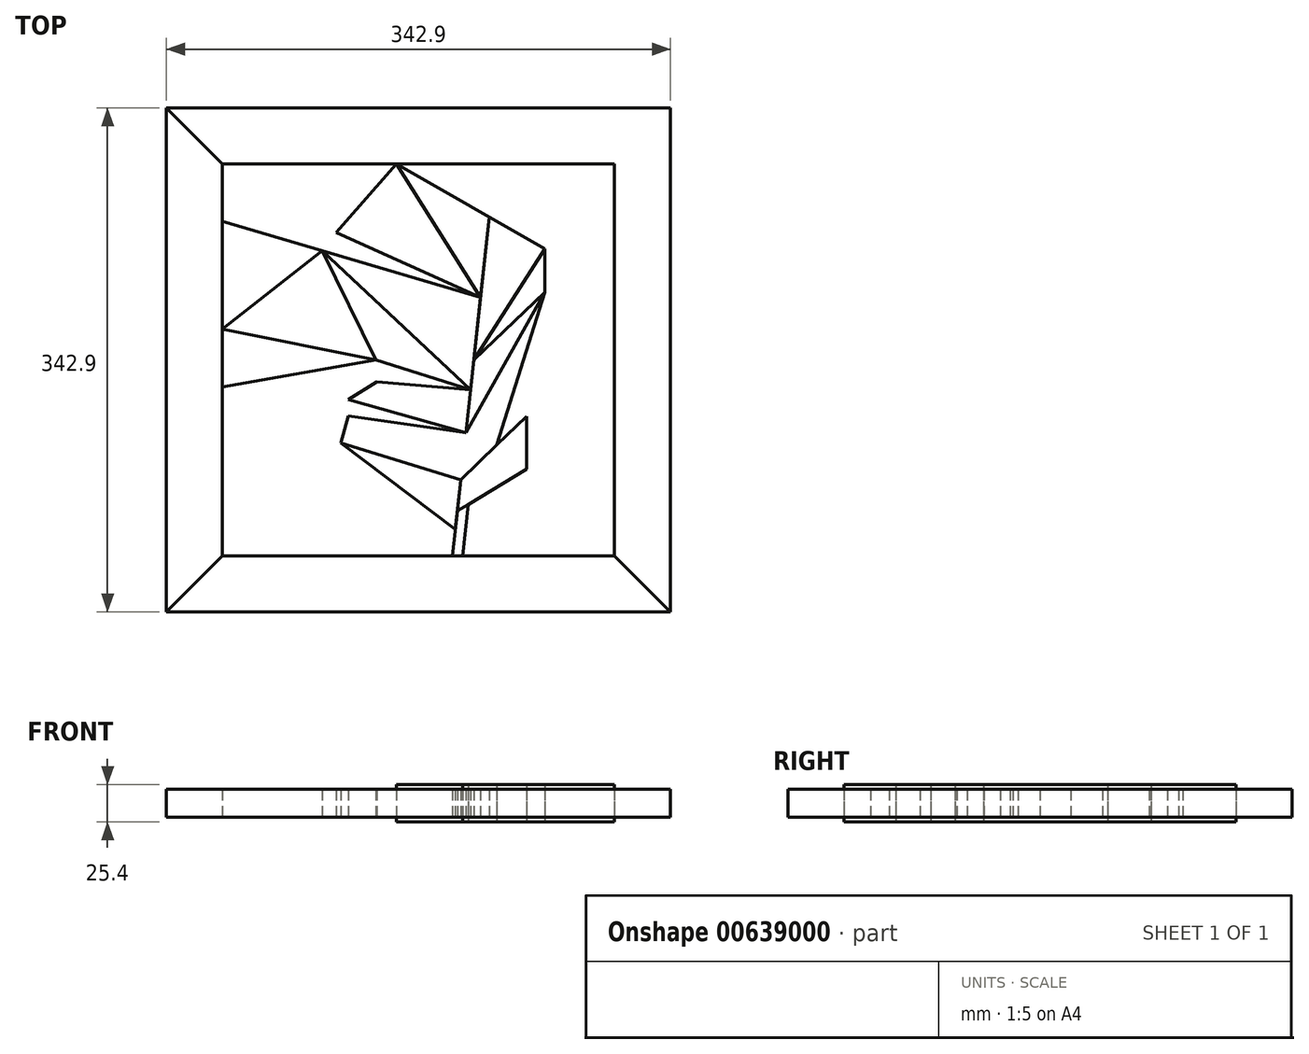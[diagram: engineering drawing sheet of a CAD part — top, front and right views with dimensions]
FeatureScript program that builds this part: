
annotation { "Feature Type Name" : "Feature", "Feature Type Description" : "" }
export const myFeature = defineFeature(function(context is Context, id is Id, definition is map)
    precondition{}
    {
        {
            var Q0;
            Q0=qCreatedBy(makeId("Top.planeOp"),FACE);
            var sketch = newSketch(context, id + "F0", { "sketchPlane" : qUnion([Q0])});
            skLineSegment(sketch, "E0.bottom", {"start": v(-171.45, -171.45) * mm, "end": v(171.45, -171.45) * mm});
            skLineSegment(sketch, "E0.top", {"start": v(-171.45, 171.45) * mm, "end": v(171.45, 171.45) * mm});
            skLineSegment(sketch, "E0.left", {"start": v(-171.45, -171.45) * mm, "end": v(-171.45, 171.45) * mm});
            skLineSegment(sketch, "E0.right", {"start": v(171.45, -171.45) * mm, "end": v(171.45, 171.45) * mm});
            skPoint(sketch, "E0.middle", {"position": v(0, 0) * mm});
            skLineSegment(sketch, "E1", {"start": v(-171.45, 171.45) * mm, "end": v(-133.35, 133.35) * mm});
            skLineSegment(sketch, "E2", {"start": v(-133.35, 133.35) * mm, "end": v(-133.35, -133.35) * mm});
            skLineSegment(sketch, "E3", {"start": v(-133.35, -133.35) * mm, "end": v(-171.45, -171.45) * mm});
            skLineSegment(sketch, "E4", {"start": v(-133.35, 133.35) * mm, "end": v(133.35, 133.35) * mm});
            skLineSegment(sketch, "E5", {"start": v(133.35, 133.35) * mm, "end": v(171.45, 171.45) * mm});
            skLineSegment(sketch, "E6", {"start": v(133.35, 133.35) * mm, "end": v(133.35, -133.35) * mm});
            skLineSegment(sketch, "E7", {"start": v(133.35, -133.35) * mm, "end": v(171.45, -171.45) * mm});
            skLineSegment(sketch, "E8", {"start": v(133.35, -133.35) * mm, "end": v(-133.35, -133.35) * mm});
            skLineSegment(sketch, "E9", {"start": v(-15.08, 133.35) * mm, "end": v(86.05, 75.46) * mm});
            skLineSegment(sketch, "E10", {"start": v(86.05, 75.46) * mm, "end": v(86.05, 45.93) * mm});
            skLineSegment(sketch, "E11", {"start": v(86.05, 45.93) * mm, "end": v(53.37, -57.95) * mm});
            skLineSegment(sketch, "E12", {"start": v(73.71, -38.4) * mm, "end": v(73.71, -74.27) * mm});
            skLineSegment(sketch, "E13", {"start": v(-15.08, 133.35) * mm, "end": v(-56.02, 86.54) * mm});
            skLineSegment(sketch, "E14", {"start": v(48.18, 97.13) * mm, "end": v(23.2, -133.35) * mm});
            skLineSegment(sketch, "E15", {"start": v(73.71, -74.27) * mm, "end": v(26.52, -102.72) * mm});
            skLineSegment(sketch, "E16", {"start": v(73.71, -38.4) * mm, "end": v(28.82, -81.55) * mm});
            skLineSegment(sketch, "E17", {"start": v(-56.02, 86.54) * mm, "end": v(42.26, 42.49) * mm});
            skLineSegment(sketch, "E18", {"start": v(-15.08, 133.35) * mm, "end": v(42.26, 42.49) * mm});
            skLineSegment(sketch, "E19", {"start": v(86.05, 75.46) * mm, "end": v(37.65, 0) * mm});
            skLineSegment(sketch, "E20", {"start": v(37.65, 0) * mm, "end": v(86.05, 45.93) * mm});
            skLineSegment(sketch, "E21", {"start": v(86.05, 45.93) * mm, "end": v(32.28, -49.6) * mm});
            skLineSegment(sketch, "E22", {"start": v(42.26, 42.49) * mm, "end": v(-65.4, 74.2) * mm});
            skLineSegment(sketch, "E23", {"start": v(-65.4, 74.2) * mm, "end": v(-28.89, 0) * mm});
            skLineSegment(sketch, "E24", {"start": v(-28.89, 0) * mm, "end": v(35.44, -20.4) * mm});
            skLineSegment(sketch, "E25", {"start": v(35.44, -20.4) * mm, "end": v(-28.32, -14.98) * mm});
            skLineSegment(sketch, "E26", {"start": v(-28.32, -14.98) * mm, "end": v(-47.63, -26.92) * mm});
            skLineSegment(sketch, "E27", {"start": v(-47.63, -26.92) * mm, "end": v(32.28, -49.6) * mm});
            skLineSegment(sketch, "E28", {"start": v(-28.32, -14.98) * mm, "end": v(32.28, -49.6) * mm});
            skLineSegment(sketch, "E29", {"start": v(-65.4, 74.2) * mm, "end": v(35.44, -20.4) * mm});
            skLineSegment(sketch, "E30", {"start": v(32.28, -49.6) * mm, "end": v(-47.63, -38.26) * mm});
            skPoint(sketch, "E30.endSnap0", {"position": v(-7.68, -38.26) * mm});
            skLineSegment(sketch, "E31", {"start": v(-47.63, -38.26) * mm, "end": v(-52.8, -56.45) * mm});
            skLineSegment(sketch, "E32", {"start": v(-52.8, -56.45) * mm, "end": v(25.16, -115.3) * mm});
            skLineSegment(sketch, "E33", {"start": v(-52.8, -56.45) * mm, "end": v(28.82, -81.55) * mm});
            skLineSegment(sketch, "E34", {"start": v(33.83, -98.31) * mm, "end": v(29.98, -133.35) * mm});
            skLineSegment(sketch, "E35", {"start": v(-56.02, 86.54) * mm, "end": v(-133.35, 94.13) * mm});
            skLineSegment(sketch, "E36", {"start": v(-133.35, 94.13) * mm, "end": v(-65.4, 74.2) * mm});
            skLineSegment(sketch, "E37", {"start": v(-65.4, 74.2) * mm, "end": v(-133.35, 21.04) * mm});
            skLineSegment(sketch, "E38", {"start": v(-133.35, 21.04) * mm, "end": v(-28.89, 0) * mm});
            skLineSegment(sketch, "E39", {"start": v(-28.89, 0) * mm, "end": v(-133.35, -18.38) * mm});
            skLineSegment(sketch, "E40", {"start": v(-133.35, -18.38) * mm, "end": v(-28.32, -14.98) * mm});
            skLineSegment(sketch, "E41", {"start": v(-56.02, 86.54) * mm, "end": v(-85.56, 133.35) * mm});
            skSolve(sketch);
        }
        {
            var Q0;
            Q0=makeQuery(id+"F0.imprint","IMPRINT",FACE,{"disambiguationData":[TD([[makeQuery(id+"F0.imprint","IMPRINT",EDGE,{"derivedFrom":sQuery(id+"F0.wireOp",EDGE,"E0.left")}),-1.0]])]});
            extrude(context, id + "F1", {"entities" : qUnion([Q0]), "depth" : 19.05 * mm, "offsetDistance" : 25.4 * mm, "symmetric" : true});
        }
        {
            var Q0;
            Q0=makeQuery(id+"F0.imprint","IMPRINT",FACE,{"disambiguationData":[TD([[makeQuery(id+"F0.imprint","IMPRINT",EDGE,{"derivedFrom":sQuery(id+"F0.wireOp",EDGE,"E0.top")}),-1.0]])]});
            extrude(context, id + "F2", {"entities" : qUnion([Q0]), "depth" : 19.05 * mm, "offsetDistance" : 25.4 * mm, "symmetric" : true});
        }
        {
            var Q0;
            Q0=makeQuery(id+"F0.imprint","IMPRINT",FACE,{"disambiguationData":[TD([[makeQuery(id+"F0.imprint","IMPRINT",EDGE,{"derivedFrom":sQuery(id+"F0.wireOp",EDGE,"E0.right")}),1.0]])]});
            extrude(context, id + "F3", {"entities" : qUnion([Q0]), "operationType" : NewBodyOperationType.ADD, "depth" : 19.05 * mm, "offsetDistance" : 25.4 * mm, "symmetric" : true});
        }
        {
            var Q0;
            Q0=makeQuery(id+"F0.imprint","IMPRINT",FACE,{"disambiguationData":[TD([[makeQuery(id+"F0.imprint","IMPRINT",EDGE,{"derivedFrom":sQuery(id+"F0.wireOp",EDGE,"E0.bottom")}),1.0]])]});
            extrude(context, id + "F4", {"entities" : qUnion([Q0]), "depth" : 19.05 * mm, "offsetDistance" : 25.4 * mm, "symmetric" : true});
        }
        {
            var Q0;
            Q0=makeQuery(id+"F0.imprint","IMPRINT",FACE,{"disambiguationData":[TD([[makeQuery(id+"F0.imprint","IMPRINT",EDGE,{"derivedFrom":sQuery(id+"F0.wireOp",EDGE,"E13")}),1.0]])]});
            extrude(context, id + "F5", {"entities" : qUnion([Q0]), "depth" : 19.05 * mm, "offsetDistance" : 25.4 * mm, "symmetric" : true});
        }
        {
            var Q0;
            {var subQ3=sQuery(id+"F0.wireOp",EDGE,"E32");Q0=makeQuery(id+"F0.imprint","IMPRINT",FACE,{"disambiguationData":[TD([[makeQuery(id+"F0.imprint","IMPRINT",EDGE,{"derivedFrom":subQ3}),1.0]])]});}
            extrude(context, id + "F6", {"entities" : qUnion([Q0]), "depth" : 19.05 * mm, "offsetDistance" : 25.4 * mm, "symmetric" : true});
        }
        {
            var Q0;
            {var subQ2=sQuery(id+"F0.wireOp",EDGE,"E12");Q0=makeQuery(id+"F0.imprint","IMPRINT",FACE,{"disambiguationData":[TD([[makeQuery(id+"F0.imprint","IMPRINT",EDGE,{"derivedFrom":subQ2}),-1.0]])]});}
            extrude(context, id + "F7", {"entities" : qUnion([Q0]), "depth" : 19.05 * mm, "offsetDistance" : 25.4 * mm, "symmetric" : true});
        }
        {
            var Q0;
            {var subQ0=sQuery(id+"F0.wireOp",EDGE,"E11");Q0=makeQuery(id+"F0.imprint","IMPRINT",FACE,{"disambiguationData":[TD([[makeQuery(id+"F0.imprint","IMPRINT",EDGE,{"derivedFrom":subQ0}),-1.0]])]});}
            extrude(context, id + "F8", {"entities" : qUnion([Q0]), "depth" : 19.05 * mm, "offsetDistance" : 25.4 * mm, "symmetric" : true});
        }
        {
            var Q0;
            {var subQ2=sQuery(id+"F0.wireOp",EDGE,"E30");Q0=makeQuery(id+"F0.imprint","IMPRINT",FACE,{"disambiguationData":[TD([[makeQuery(id+"F0.imprint","IMPRINT",EDGE,{"derivedFrom":subQ2}),1.0]])]});}
            extrude(context, id + "F9", {"entities" : qUnion([Q0]), "depth" : 19.05 * mm, "offsetDistance" : 25.4 * mm, "symmetric" : true});
        }
        {
            var Q0;
            Q0=makeQuery(id+"F0.imprint","IMPRINT",FACE,{"disambiguationData":[TD([[makeQuery(id+"F0.imprint","IMPRINT",EDGE,{"derivedFrom":sQuery(id+"F0.wireOp",EDGE,"E26")}),1.0]])]});
            extrude(context, id + "F10", {"entities" : qUnion([Q0]), "depth" : 19.05 * mm, "offsetDistance" : 25.4 * mm, "symmetric" : true});
        }
        {
            var Q0;
            {var subQ2=sQuery(id+"F0.wireOp",EDGE,"E25");Q0=makeQuery(id+"F0.imprint","IMPRINT",FACE,{"disambiguationData":[TD([[makeQuery(id+"F0.imprint","IMPRINT",EDGE,{"derivedFrom":subQ2}),1.0]])]});}
            extrude(context, id + "F11", {"entities" : qUnion([Q0]), "operationType" : NewBodyOperationType.ADD, "depth" : 19.05 * mm, "offsetDistance" : 25.4 * mm, "symmetric" : true});
        }
        {
            var Q0;
            {var subQ0=sQuery(id+"F0.wireOp",EDGE,"E20");Q0=makeQuery(id+"F0.imprint","IMPRINT",FACE,{"disambiguationData":[TD([[makeQuery(id+"F0.imprint","IMPRINT",EDGE,{"derivedFrom":subQ0}),-1.0]])]});}
            extrude(context, id + "F12", {"entities" : qUnion([Q0]), "depth" : 19.05 * mm, "offsetDistance" : 25.4 * mm, "symmetric" : true});
        }
        {
            var Q0;
            Q0=makeQuery(id+"F0.imprint","IMPRINT",FACE,{"disambiguationData":[TD([[makeQuery(id+"F0.imprint","IMPRINT",EDGE,{"derivedFrom":sQuery(id+"F0.wireOp",EDGE,"E10")}),-1.0]])]});
            extrude(context, id + "F13", {"entities" : qUnion([Q0]), "depth" : 19.05 * mm, "offsetDistance" : 25.4 * mm, "symmetric" : true});
        }
        {
            var Q0;
            {var subQ0=sQuery(id+"F0.wireOp",EDGE,"E19");Q0=makeQuery(id+"F0.imprint","IMPRINT",FACE,{"disambiguationData":[TD([[makeQuery(id+"F0.imprint","IMPRINT",EDGE,{"derivedFrom":subQ0}),-1.0]])]});}
            extrude(context, id + "F14", {"entities" : qUnion([Q0]), "depth" : 19.05 * mm, "offsetDistance" : 25.4 * mm, "symmetric" : true});
        }
        {
            var Q0;
            {var subQ0=sQuery(id+"F0.wireOp",EDGE,"E18");Q0=makeQuery(id+"F0.imprint","IMPRINT",FACE,{"disambiguationData":[TD([[makeQuery(id+"F0.imprint","IMPRINT",EDGE,{"derivedFrom":subQ0}),1.0]])]});}
            extrude(context, id + "F15", {"entities" : qUnion([Q0]), "depth" : 19.05 * mm, "offsetDistance" : 25.4 * mm, "symmetric" : true});
        }
        {
            var Q0;
            {var subQ0=sQuery(id+"F0.wireOp",EDGE,"E22");Q0=makeQuery(id+"F0.imprint","IMPRINT",FACE,{"disambiguationData":[TD([[makeQuery(id+"F0.imprint","IMPRINT",EDGE,{"derivedFrom":subQ0}),1.0]])]});}
            extrude(context, id + "F16", {"entities" : qUnion([Q0]), "depth" : 19.05 * mm, "offsetDistance" : 25.4 * mm, "symmetric" : true});
        }
        {
            var Q0;
            Q0=makeQuery(id+"F0.imprint","IMPRINT",FACE,{"disambiguationData":[TD([[makeQuery(id+"F0.imprint","IMPRINT",EDGE,{"derivedFrom":sQuery(id+"F0.wireOp",EDGE,"E23")}),1.0]])]});
            extrude(context, id + "F17", {"entities" : qUnion([Q0]), "depth" : 19.05 * mm, "offsetDistance" : 25.4 * mm, "symmetric" : true});
        }
        {
            var Q0;
            {var subQ3=sQuery(id+"F0.wireOp",EDGE,"E34");Q0=makeQuery(id+"F0.imprint","IMPRINT",FACE,{"disambiguationData":[TD([[makeQuery(id+"F0.imprint","IMPRINT",EDGE,{"derivedFrom":subQ3}),-1.0]])]});}
            extrude(context, id + "F18", {"entities" : qUnion([Q0]), "depth" : 19.05 * mm, "offsetDistance" : 25.4 * mm, "symmetric" : true});
        }
        {
            var Q0;
            {var subQ4=sQuery(id+"F0.wireOp",EDGE,"E2");Q0=makeQuery(id+"F0.imprint","IMPRINT",FACE,{"disambiguationData":[TD([[makeQuery(id+"F0.imprint","IMPRINT",EDGE,{"derivedFrom":subQ4}),1.0]])]});}
            extrude(context, id + "F19", {"entities" : qUnion([Q0]), "depth" : 19.05 * mm, "offsetDistance" : 25.4 * mm, "symmetric" : true});
        }
        {
            var Q0;
            {var subQ3=sQuery(id+"F0.wireOp",EDGE,"E6");Q0=makeQuery(id+"F0.imprint","IMPRINT",FACE,{"disambiguationData":[TD([[makeQuery(id+"F0.imprint","IMPRINT",EDGE,{"derivedFrom":subQ3}),-1.0]])]});}
            extrude(context, id + "F20", {"entities" : qUnion([Q0]), "depth" : 25.4 * mm, "offsetDistance" : 25.4 * mm, "symmetric" : true});
        }
    });
